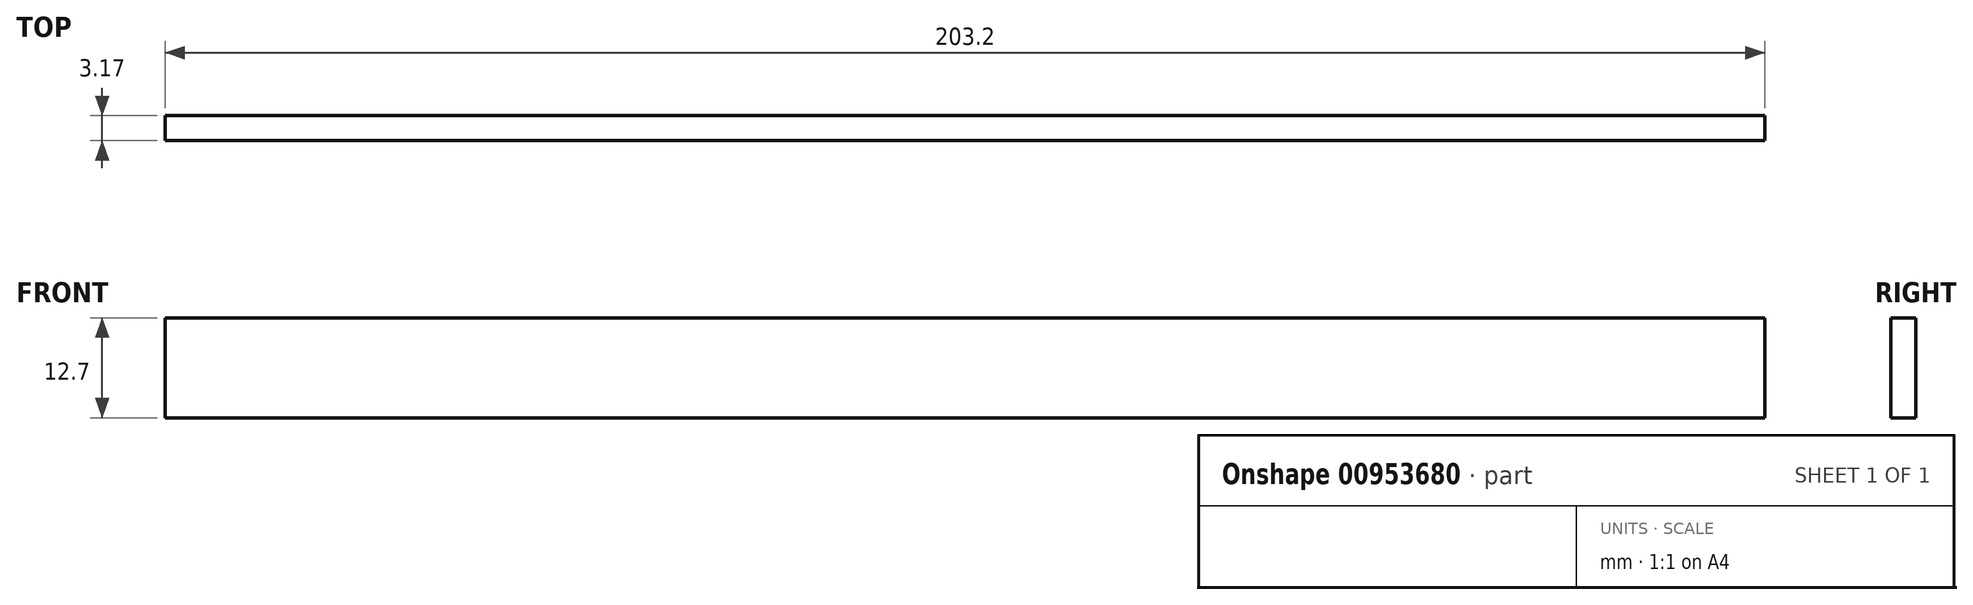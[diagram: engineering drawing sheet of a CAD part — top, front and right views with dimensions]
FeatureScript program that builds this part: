
annotation { "Feature Type Name" : "Feature", "Feature Type Description" : "" }
export const myFeature = defineFeature(function(context is Context, id is Id, definition is map)
    precondition{}
    {
        {
            var Q0;
            Q0=qCreatedBy(makeId("Front.planeOp"),FACE);
            var sketch = newSketch(context, id + "F0", { "sketchPlane" : qUnion([Q0])});
            skLineSegment(sketch, "E0.bottom", {"start": v(-95.2, 6.07) * mm, "end": v(108, 6.07) * mm});
            skLineSegment(sketch, "E0.top", {"start": v(-95.2, -6.63) * mm, "end": v(108, -6.63) * mm});
            skLineSegment(sketch, "E0.left", {"start": v(-95.2, 6.07) * mm, "end": v(-95.2, -6.63) * mm});
            skLineSegment(sketch, "E0.right", {"start": v(108, 6.07) * mm, "end": v(108, -6.63) * mm});
            skSolve(sketch);
        }
        {
            var Q0;
            Q0 = qSketchRegion(id + "F0", true);
            extrude(context, id + "F1", {"entities" : qUnion([Q0]), "depth" : 3.17 * mm, "offsetDistance" : 25.4 * mm});
        }
    });
